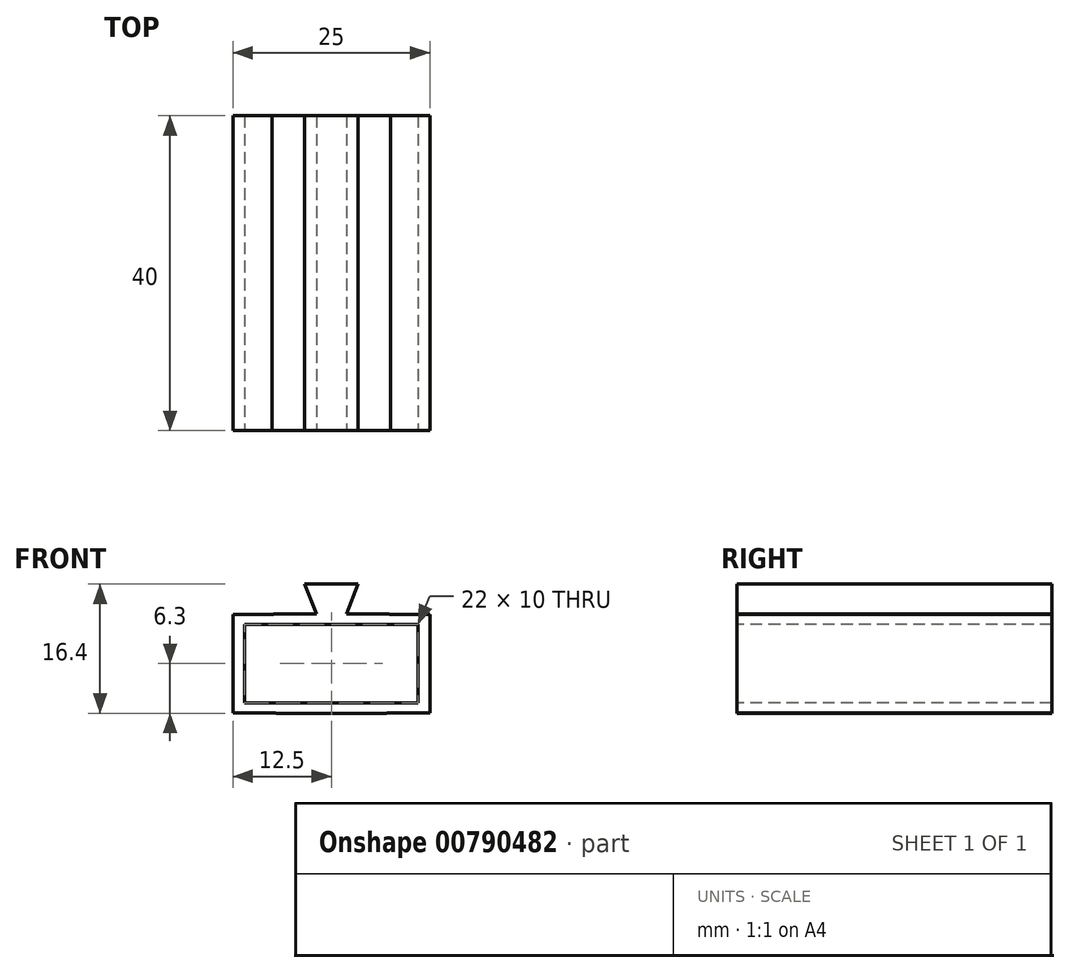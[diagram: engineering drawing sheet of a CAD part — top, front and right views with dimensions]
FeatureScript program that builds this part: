
annotation { "Feature Type Name" : "Feature", "Feature Type Description" : "" }
export const myFeature = defineFeature(function(context is Context, id is Id, definition is map)
    precondition{}
    {
        {
            var Q0;
            Q0=qCreatedBy(makeId("Top.planeOp"),FACE);
            var sketch = newSketch(context, id + "F0", { "sketchPlane" : qUnion([Q0])});
            skLineSegment(sketch, "E0.bottom", {"start": v(9.35, 19.25) * mm, "end": v(-9.35, 19.25) * mm});
            skLineSegment(sketch, "E0.top", {"start": v(9.35, -19.25) * mm, "end": v(-9.35, -19.25) * mm});
            skLineSegment(sketch, "E0.left", {"start": v(9.35, 19.25) * mm, "end": v(9.35, -19.25) * mm});
            skLineSegment(sketch, "E0.right", {"start": v(-9.35, 19.25) * mm, "end": v(-9.35, -19.25) * mm});
            skPoint(sketch, "E0.middle", {"position": v(0, 0) * mm});
            skSolve(sketch);
        }
        {
            var Q0;
            Q0=qSketchRegion(id+"F0",true);
            extrude(context, id + "F1", {"entities" : qUnion([Q0]), "depth" : 8 * mm, "offsetDistance" : 25 * mm});
        }
        {
            var Q0;
            Q0=makeQuery(id+"F1.opExtrude","CAP_EDGE",EDGE,{"disambiguationData":[OSD([sQuery(id+"F0.wireOp",EDGE,"E0.left")])],"isStart":false});
            var Q1;
            Q1=makeQuery(id+"F1.opExtrude","CAP_EDGE",EDGE,{"disambiguationData":[OSD([sQuery(id+"F0.wireOp",EDGE,"E0.left")])],"isStart":true});
            var Q2;
            Q2=makeQuery(id+"F1.opExtrude","CAP_EDGE",EDGE,{"disambiguationData":[OSD([sQuery(id+"F0.wireOp",EDGE,"E0.right")])],"isStart":false});
            var Q3;
            Q3=makeQuery(id+"F1.opExtrude","CAP_EDGE",EDGE,{"disambiguationData":[OSD([sQuery(id+"F0.wireOp",EDGE,"E0.right")])],"isStart":true});
            fillet(context, id + "F2", {"entities" : qUnion([Q0, Q1, Q2, Q3]), "radius" : 2.5 * mm, "tangentPropagation" : true, "allowEdgeOverflow" : false});
        }
        {
            var Q0;
            Q0=makeQuery(id+"F1.opExtrude","SWEPT_FACE",FACE,{"disambiguationData":[OSD([sQuery(id+"F0.wireOp",EDGE,"E0.top")])]});
            var sketch = newSketch(context, id + "F3", { "sketchPlane" : qUnion([Q0])});
            skLineSegment(sketch, "E1.0", {"start": v(6.85, 8.3) * mm, "end": v(-6.85, 8.3) * mm});
            skArc(sketch, "E2.0", {"start": v(9.65, 5.5) * mm, "mid": v(8.83, 7.48) * mm, "end": v(6.85, 8.3) * mm});
            skLineSegment(sketch, "E3.0", {"start": v(9.65, 5.5) * mm, "end": v(9.65, 2.5) * mm});
            skArc(sketch, "E4.0", {"start": v(6.85, -0.3) * mm, "mid": v(8.83, 0.52) * mm, "end": v(9.65, 2.5) * mm});
            skLineSegment(sketch, "E5.0", {"start": v(6.85, -0.3) * mm, "end": v(-6.85, -0.3) * mm});
            skArc(sketch, "E6.0", {"start": v(-9.65, 2.5) * mm, "mid": v(-8.83, 0.52) * mm, "end": v(-6.85, -0.3) * mm});
            skLineSegment(sketch, "E7.0", {"start": v(-9.65, 5.5) * mm, "end": v(-9.65, 2.5) * mm});
            skArc(sketch, "E8.0", {"start": v(-6.85, 8.3) * mm, "mid": v(-8.83, 7.48) * mm, "end": v(-9.65, 5.5) * mm});
            skArc(sketch, "E9.0", {"start": v(-11.65, 2.5) * mm, "mid": v(-10.24, -0.9) * mm, "end": v(-6.85, -2.3) * mm});
            skLineSegment(sketch, "E9.1", {"start": v(-11.65, 5.5) * mm, "end": v(-11.65, 2.5) * mm});
            skLineSegment(sketch, "E9.2", {"start": v(-6.85, -2.3) * mm, "end": v(6.85, -2.3) * mm});
            skArc(sketch, "E9.3", {"start": v(-6.85, 10.3) * mm, "mid": v(-10.24, 8.9) * mm, "end": v(-11.65, 5.5) * mm});
            skArc(sketch, "E9.4", {"start": v(6.85, -2.3) * mm, "mid": v(10.24, -0.9) * mm, "end": v(11.65, 2.5) * mm});
            skLineSegment(sketch, "E9.5", {"start": v(11.65, 2.5) * mm, "end": v(11.65, 5.5) * mm});
            skArc(sketch, "E9.6", {"start": v(11.65, 5.5) * mm, "mid": v(10.24, 8.9) * mm, "end": v(6.85, 10.3) * mm});
            skLineSegment(sketch, "E9.7", {"start": v(6.85, 10.3) * mm, "end": v(-6.85, 10.3) * mm});
            skSolve(sketch);
        }
        {
            var Q0;
            Q0=qSketchRegion(id+"F3",true);
            extrude(context, id + "F4", {"entities" : qUnion([Q0]), "oppositeDirection" : true, "depth" : 40 * mm, "offsetDistance" : 25 * mm});
        }
        {
            var Q0;
            Q0=makeQuery(id+"F1.opExtrude","SWEPT_BODY",BODY,{"disambiguationData":[OSD([sQuery(id+"F0.wireOp",EDGE,"E0.bottom"),sQuery(id+"F0.wireOp",EDGE,"E0.top"),sQuery(id+"F0.wireOp",EDGE,"E0.left"),sQuery(id+"F0.wireOp",EDGE,"E0.right")])]});
            deleteBodies(context, id + "F5", {"entities" : qUnion([Q0])});
        }
        {
            var Q0;
            Q0=makeQuery(id+"F4.opExtrude","CAP_FACE",FACE,{"disambiguationData":[OSD([sQuery(id+"F3.wireOp",EDGE,"E1.0"),sQuery(id+"F3.wireOp",EDGE,"E2.0"),sQuery(id+"F3.wireOp",EDGE,"E3.0"),sQuery(id+"F3.wireOp",EDGE,"E4.0"),sQuery(id+"F3.wireOp",EDGE,"E5.0"),sQuery(id+"F3.wireOp",EDGE,"E6.0"),sQuery(id+"F3.wireOp",EDGE,"E7.0"),sQuery(id+"F3.wireOp",EDGE,"E8.0"),sQuery(id+"F3.wireOp",EDGE,"E9.0"),sQuery(id+"F3.wireOp",EDGE,"E9.1"),sQuery(id+"F3.wireOp",EDGE,"E9.2"),sQuery(id+"F3.wireOp",EDGE,"E9.3"),sQuery(id+"F3.wireOp",EDGE,"E9.4"),sQuery(id+"F3.wireOp",EDGE,"E9.5"),sQuery(id+"F3.wireOp",EDGE,"E9.6"),sQuery(id+"F3.wireOp",EDGE,"E9.7")])],"isStart":true});
            var sketch = newSketch(context, id + "F6", { "sketchPlane" : qUnion([Q0])});
            skLineSegment(sketch, "E10.top", {"start": v(1.9, 14.1) * mm, "end": v(-1.9, 14.1) * mm});
            skPoint(sketch, "E10.middle", {"position": v(0, 10.3) * mm});
            skLineSegment(sketch, "E11", {"start": v(-1.9, 10.3) * mm, "end": v(1.9, 10.3) * mm});
            skPoint(sketch, "E10.bottom.end.orphan", {"position": v(-3.4, 6.5) * mm});
            skPoint(sketch, "E12.orphan", {"position": v(3.4, 6.5) * mm});
            skPoint(sketch, "E13", {"position": v(-1.9, 14.1) * mm});
            skPoint(sketch, "E14", {"position": v(1.9, 14.1) * mm});
            skPoint(sketch, "E10.right.end.orphan", {"position": v(-3.4, 14.1) * mm});
            skPoint(sketch, "E10.left.end.orphan", {"position": v(3.4, 14.1) * mm});
            skLineSegment(sketch, "E15", {"start": v(-1.9, 10.3) * mm, "end": v(-3.4, 14.1) * mm});
            skLineSegment(sketch, "E16", {"start": v(1.9, 10.3) * mm, "end": v(3.4, 14.1) * mm});
            skLineSegment(sketch, "E17", {"start": v(-3.4, 14.1) * mm, "end": v(-1.9, 14.1) * mm});
            skLineSegment(sketch, "E18", {"start": v(1.9, 14.1) * mm, "end": v(3.4, 14.1) * mm});
            skPoint(sketch, "E19.orphan", {"position": v(-3.4, 10.3) * mm});
            skPoint(sketch, "E20.orphan", {"position": v(3.4, 10.3) * mm});
            skSolve(sketch);
        }
        {
            var Q0;
            Q0=qSketchRegion(id+"F6",true);
            extrude(context, id + "F7", {"entities" : qUnion([Q0]), "operationType" : NewBodyOperationType.ADD, "oppositeDirection" : true, "depth" : 40 * mm, "offsetDistance" : 25 * mm});
        }
        {
            var Q0;
            Q0=makeQuery(id+"F7.boolean.opBoolean","MERGE",FACE,{"derivedFrom":[makeQuery(id+"F4.opExtrude","CAP_FACE",FACE,{"disambiguationData":[OSD([sQuery(id+"F3.wireOp",EDGE,"E1.0"),sQuery(id+"F3.wireOp",EDGE,"E2.0"),sQuery(id+"F3.wireOp",EDGE,"E3.0"),sQuery(id+"F3.wireOp",EDGE,"E4.0"),sQuery(id+"F3.wireOp",EDGE,"E5.0"),sQuery(id+"F3.wireOp",EDGE,"E6.0"),sQuery(id+"F3.wireOp",EDGE,"E7.0"),sQuery(id+"F3.wireOp",EDGE,"E8.0"),sQuery(id+"F3.wireOp",EDGE,"E9.0"),sQuery(id+"F3.wireOp",EDGE,"E9.1"),sQuery(id+"F3.wireOp",EDGE,"E9.2"),sQuery(id+"F3.wireOp",EDGE,"E9.3"),sQuery(id+"F3.wireOp",EDGE,"E9.4"),sQuery(id+"F3.wireOp",EDGE,"E9.5"),sQuery(id+"F3.wireOp",EDGE,"E9.6"),sQuery(id+"F3.wireOp",EDGE,"E9.7")])],"isStart":true}),makeQuery(id+"F7.opExtrude","CAP_FACE",FACE,{"disambiguationData":[OSD([sQuery(id+"F6.wireOp",EDGE,"E10.top"),sQuery(id+"F6.wireOp",EDGE,"E11"),sQuery(id+"F6.wireOp",EDGE,"E15"),sQuery(id+"F6.wireOp",EDGE,"E16"),sQuery(id+"F6.wireOp",EDGE,"E17"),sQuery(id+"F6.wireOp",EDGE,"E18")])],"isStart":true})]});
            var sketch = newSketch(context, id + "F8", { "sketchPlane" : qUnion([Q0])});
            skLineSegment(sketch, "E21.bottom", {"start": v(12.5, 10.25) * mm, "end": v(-12.5, 10.25) * mm});
            skLineSegment(sketch, "E21.top", {"start": v(12.5, -2.25) * mm, "end": v(-12.5, -2.25) * mm});
            skLineSegment(sketch, "E21.left", {"start": v(12.5, 10.25) * mm, "end": v(12.5, -2.25) * mm});
            skLineSegment(sketch, "E21.right", {"start": v(-12.5, 10.25) * mm, "end": v(-12.5, -2.25) * mm});
            skPoint(sketch, "E21.middle", {"position": v(0, 4) * mm});
            skPoint(sketch, "E21.middle.positionSnap0", {"position": v(9.65, 4) * mm});
            skPoint(sketch, "E21.centerSnap0", {"position": v(9.65, 4) * mm});
            skSolve(sketch);
        }
        {
            var Q0;
            Q0=qSketchRegion(id+"F8",true);
            extrude(context, id + "F9", {"entities" : qUnion([Q0]), "operationType" : NewBodyOperationType.ADD, "oppositeDirection" : true, "depth" : 40 * mm, "offsetDistance" : 25 * mm});
        }
        {
            var Q0;
            Q0=makeQuery(id+"F9.boolean.opBoolean","MERGE",FACE,{"derivedFrom":[makeQuery(id+"F7.boolean.opBoolean","MERGE",FACE,{"derivedFrom":[makeQuery(id+"F4.opExtrude","CAP_FACE",FACE,{"disambiguationData":[OSD([sQuery(id+"F3.wireOp",EDGE,"E1.0"),sQuery(id+"F3.wireOp",EDGE,"E2.0"),sQuery(id+"F3.wireOp",EDGE,"E3.0"),sQuery(id+"F3.wireOp",EDGE,"E4.0"),sQuery(id+"F3.wireOp",EDGE,"E5.0"),sQuery(id+"F3.wireOp",EDGE,"E6.0"),sQuery(id+"F3.wireOp",EDGE,"E7.0"),sQuery(id+"F3.wireOp",EDGE,"E8.0"),sQuery(id+"F3.wireOp",EDGE,"E9.0"),sQuery(id+"F3.wireOp",EDGE,"E9.1"),sQuery(id+"F3.wireOp",EDGE,"E9.2"),sQuery(id+"F3.wireOp",EDGE,"E9.3"),sQuery(id+"F3.wireOp",EDGE,"E9.4"),sQuery(id+"F3.wireOp",EDGE,"E9.5"),sQuery(id+"F3.wireOp",EDGE,"E9.6"),sQuery(id+"F3.wireOp",EDGE,"E9.7")])],"isStart":true}),makeQuery(id+"F7.opExtrude","CAP_FACE",FACE,{"disambiguationData":[OSD([sQuery(id+"F6.wireOp",EDGE,"E10.top"),sQuery(id+"F6.wireOp",EDGE,"E11"),sQuery(id+"F6.wireOp",EDGE,"E15"),sQuery(id+"F6.wireOp",EDGE,"E16"),sQuery(id+"F6.wireOp",EDGE,"E17"),sQuery(id+"F6.wireOp",EDGE,"E18")])],"isStart":true})]}),makeQuery(id+"F9.opExtrude","CAP_FACE",FACE,{"disambiguationData":[OSD([sQuery(id+"F8.wireOp",EDGE,"E21.bottom"),sQuery(id+"F8.wireOp",EDGE,"E21.top"),sQuery(id+"F8.wireOp",EDGE,"E21.left"),sQuery(id+"F8.wireOp",EDGE,"E21.right")])],"isStart":true})]});
            var sketch = newSketch(context, id + "F10", { "sketchPlane" : qUnion([Q0])});
            skLineSegment(sketch, "E22.bottom", {"start": v(11, 9) * mm, "end": v(-11, 9) * mm});
            skLineSegment(sketch, "E22.top", {"start": v(11, -1) * mm, "end": v(-11, -1) * mm});
            skLineSegment(sketch, "E22.left", {"start": v(11, 9) * mm, "end": v(11, -1) * mm});
            skLineSegment(sketch, "E22.right", {"start": v(-11, 9) * mm, "end": v(-11, -1) * mm});
            skPoint(sketch, "E22.middle", {"position": v(0, 4) * mm});
            skPoint(sketch, "E22.middle.positionSnap0", {"position": v(12.5, 4) * mm});
            skPoint(sketch, "E22.centerSnap0", {"position": v(12.5, 4) * mm});
            skSolve(sketch);
        }
        {
            var Q0;
            Q0=qSketchRegion(id+"F10",true);
            extrude(context, id + "F11", {"entities" : qUnion([Q0]), "operationType" : NewBodyOperationType.REMOVE, "oppositeDirection" : true, "depth" : 40 * mm, "offsetDistance" : 25 * mm});
        }
    });
